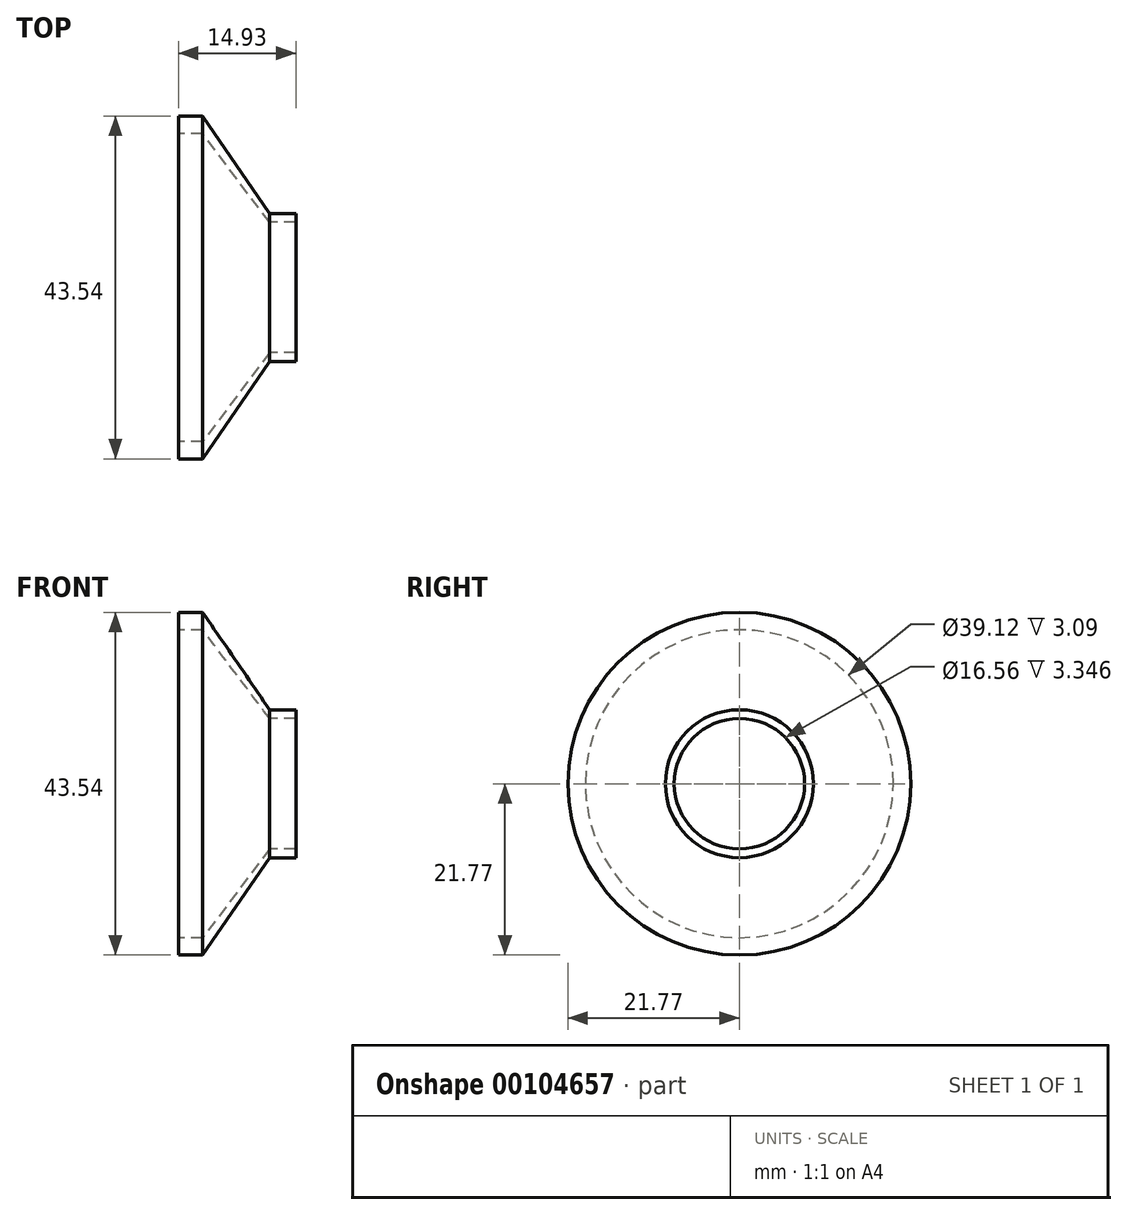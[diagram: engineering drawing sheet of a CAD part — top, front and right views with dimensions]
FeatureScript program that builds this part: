
annotation { "Feature Type Name" : "Feature", "Feature Type Description" : "" }
export const myFeature = defineFeature(function(context is Context, id is Id, definition is map)
    precondition{}
    {
        {
            var Q0;
            Q0=qCreatedBy(makeId("Top.planeOp"),FACE);
            var sketch = newSketch(context, id + "F0", { "sketchPlane" : qUnion([Q0])});
            skLineSegment(sketch, "E0", {"start": v(-14.93, 21.77) * mm, "end": v(-11.84, 21.77) * mm});
            skLineSegment(sketch, "E1", {"start": v(-11.84, 21.77) * mm, "end": v(-3.35, 9.4) * mm});
            skLineSegment(sketch, "E2", {"start": v(-3.35, 9.4) * mm, "end": v(0, 9.4) * mm});
            skLineSegment(sketch, "E3", {"start": v(0, 9.4) * mm, "end": v(0, 8.28) * mm});
            skLineSegment(sketch, "E4", {"start": v(0, 8.28) * mm, "end": v(-3.35, 8.28) * mm});
            skLineSegment(sketch, "E5", {"start": v(-3.35, 8.28) * mm, "end": v(-11.84, 19.56) * mm});
            skLineSegment(sketch, "E6", {"start": v(-11.84, 19.56) * mm, "end": v(-14.93, 19.56) * mm});
            skLineSegment(sketch, "E7", {"start": v(-14.93, 19.56) * mm, "end": v(-14.93, 21.77) * mm});
            skLineSegment(sketch, "E8", {"start": v(-41.3, 0) * mm, "end": v(54, 0) * mm, "construction": true});
            skSolve(sketch);
        }
        {
            var Q0;
            Q0=makeQuery(id+"F0.imprint","IMPRINT",FACE,{"disambiguationData":[TD([[makeQuery(id+"F0.imprint","IMPRINT",EDGE,{"derivedFrom":sQuery(id+"F0.wireOp",EDGE,"E0")}),-1.0]])]});
            var Q1;
            Q1=sQuery(id+"F0.wireOp",EDGE,"E8");
            revolve(context, id + "F1", {"entities" : qUnion([Q0]), "axis" : qUnion([Q1]), "revolveType" : RevolveType.FULL});
        }
    });
